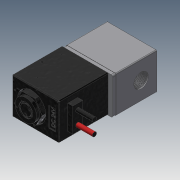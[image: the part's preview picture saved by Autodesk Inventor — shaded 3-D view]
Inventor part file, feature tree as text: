
AUTODESK INVENTOR PART (.ipt)
format: ipt  version: 2020.3 (Build 243373000, 373)  size: 1,473,024 bytes
history: native  units: in
note: dims shown in document units (in); Inventor stores cm internally (conversion verified against a paired STEP export)
features: fillet x2, thread x1
ambient origin geometry x8: Origin, YZ Plane, XZ Plane, XY Plane, X Axis, Y Axis, Z Axis, Center Point
bodies: Solid1 (feature_tree), Solid2 (feature_tree), Solid3 (feature_tree)
feature tree (3):
  fillet  "Fillet3"  [1 undecoded]
  thread  "Thread4"  [1 undecoded]
  fillet  "Fillet5"  [1 undecoded]
note: 3 required parameter values undecoded (feature->parameter linkage not recoverable at this tier; creation-order binding heuristic only, values carry confidence <= 0.55)
